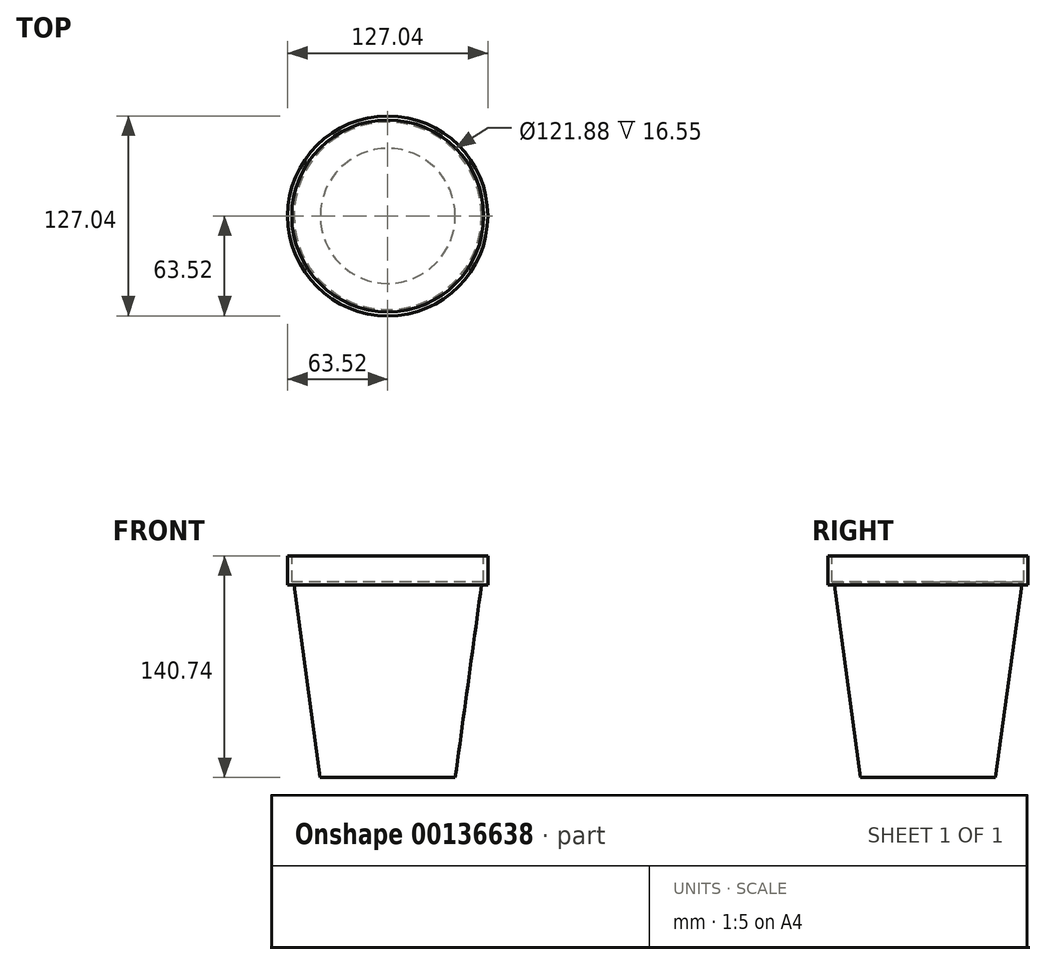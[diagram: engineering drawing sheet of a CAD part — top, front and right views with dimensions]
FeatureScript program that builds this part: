
annotation { "Feature Type Name" : "Feature", "Feature Type Description" : "" }
export const myFeature = defineFeature(function(context is Context, id is Id, definition is map)
    precondition{}
    {
        {
            var Q0;
            Q0=qCreatedBy(makeId("Front.planeOp"),FACE);
            var sketch = newSketch(context, id + "F0", { "sketchPlane" : qUnion([Q0])});
            skLineSegment(sketch, "E0", {"start": v(0, -46.66) * mm, "end": v(42.86, -46.66) * mm});
            skLineSegment(sketch, "E1", {"start": v(42.86, -46.66) * mm, "end": v(59.52, 75.67) * mm});
            skLineSegment(sketch, "E2", {"start": v(59.52, 75.67) * mm, "end": v(63.52, 75.67) * mm});
            skLineSegment(sketch, "E3", {"start": v(63.52, 75.67) * mm, "end": v(63.52, 94.08) * mm});
            skLineSegment(sketch, "E4", {"start": v(63.52, 94.08) * mm, "end": v(0, 94.08) * mm});
            skLineSegment(sketch, "E5", {"start": v(0, 94.08) * mm, "end": v(0, -46.66) * mm});
            skSolve(sketch);
        }
        {
            var Q0;
            Q0=makeQuery(id+"F0.imprint","IMPRINT",FACE,{"disambiguationData":[TD([[makeQuery(id+"F0.imprint","IMPRINT",EDGE,{"derivedFrom":sQuery(id+"F0.wireOp",EDGE,"E0")}),1.0]])]});
            var Q1;
            Q1=sQuery(id+"F0.wireOp",EDGE,"E5");
            revolve(context, id + "F1", {"entities" : qUnion([Q0]), "axis" : qUnion([Q1]), "revolveType" : RevolveType.FULL});
        }
        {
            var Q0;
            Q0=makeQuery(id+"F1.opRevolve","SWEPT_FACE",FACE,{"disambiguationData":[OSD([sQuery(id+"F0.wireOp",EDGE,"E4")])]});
            var sketch = newSketch(context, id + "F2", { "sketchPlane" : qUnion([Q0])});
            skPoint(sketch, "E6", {"position": v(0, 0) * mm});
            skCircle(sketch, "E7", {"center": v(0, 0) * mm, "radius": 60.94 * mm});
            skSolve(sketch);
        }
        {
            var Q0;
            Q0=makeQuery(id+"F2.imprint","IMPRINT",FACE,{"disambiguationData":[TD([[makeQuery(id+"F2.imprint","IMPRINT",EDGE,{"derivedFrom":sQuery(id+"F2.wireOp",EDGE,"E7")}),1.0]])]});
            extrude(context, id + "F3", {"entities" : qUnion([Q0]), "operationType" : NewBodyOperationType.REMOVE, "oppositeDirection" : true, "depth" : 16.55 * mm});
        }
    });
